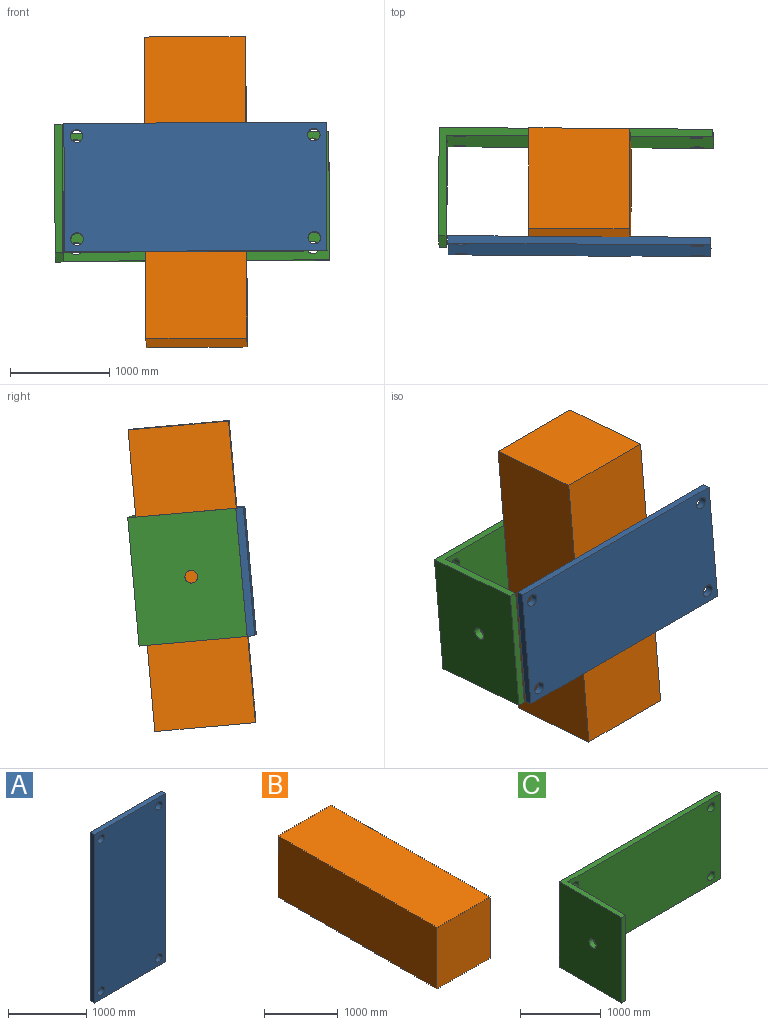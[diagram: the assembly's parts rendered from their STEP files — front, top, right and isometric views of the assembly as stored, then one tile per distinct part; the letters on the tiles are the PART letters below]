
ASSEMBLY  parts=3 mates=2
PART A: 10 faces, bbox 1295.4x76.2x2641.6 mm
  f0: plane 1295.4x76.2mm, normal (0,0,1), area 98709.5mm2, adj f1,f3,f4,f5
  f1: plane 2641.6x76.2mm, normal (-1,0,0), area 201289.9mm2, adj f0,f2,f4,f5
  f2: plane 1295.4x76.2mm, normal (0,0,-1), area 98709.5mm2, adj f1,f3,f4,f5
  f3: plane 2641.6x76.2mm, normal (1,0,0), area 201289.9mm2, adj f0,f2,f4,f5
  f4: plane 2641.6x1295.4mm, normal (0,-1,0), area 3371257.9mm2, adj f0,f1,f2,f3,f6,f7,f8,f9
  f5: plane 2641.6x1295.4mm, normal (0,1,0), area 3371257.9mm2, adj f0,f1,f2,f3,f6,f7,f8,f9
  f6: cylinder r=63.5mm len=127mm, axis (0,1,0), area 30402.4mm2, adj f4,f5
  f7: cylinder r=63.5mm len=127mm, axis (0,1,0), area 30402.4mm2, adj f4,f5
  f8: cylinder r=63.5mm len=127mm, axis (0,1,0), area 30402.4mm2, adj f4,f5
  f9: cylinder r=63.5mm len=127mm, axis (0,1,0), area 30402.4mm2, adj f4,f5
PART B: 6 faces, bbox 1016x3048x1016 mm
  f0: plane 3048x1016mm, normal (0,0,1), area 3096768mm2, adj f1,f3,f4,f5
  f1: plane 3048x1016mm, normal (-1,0,0), area 3096768mm2, adj f0,f2,f4,f5
  f2: plane 3048x1016mm, normal (0,0,-1), area 3096768mm2, adj f1,f3,f4,f5
  f3: plane 3048x1016mm, normal (1,0,0), area 3096768mm2, adj f0,f2,f4,f5
  f4: plane 1016x1016mm, normal (0,-1,0), area 1032256mm2, adj f0,f1,f2,f3
  f5: plane 1016x1016mm, normal (0,1,0), area 1032256mm2, adj f0,f1,f2,f3
PART C: 13 faces, bbox 2754.9x1092.2x1295.4 mm
  f0: plane 2678.71x1295.4mm, normal (0,-1,0), area 3419330.9mm2, adj f1,f3,f4,f6,f7,f8,f9,f10
  f1: plane 2754.91x1092.2mm, normal (0,0,1), area 287343.4mm2, adj f0,f2,f4,f5,f10,f11
  f2: plane 1295.4x1092.2mm, normal (-1,0,0), area 1402168.2mm2, adj f1,f3,f5,f11,f12
  f3: plane 2754.91x1092.2mm, normal (0,0,-1), area 287343.4mm2, adj f0,f2,f4,f5,f10,f11
  f4: plane 1295.4x76.2mm, normal (1,0,0), area 98709.5mm2, adj f0,f1,f3,f5
  f5: plane 2754.91x1295.4mm, normal (0,1,0), area 3518040.4mm2, adj f1,f2,f3,f4,f6,f7,f8,f9
  f6: cylinder r=63.5mm len=127mm, axis (0,1,0), area 30402.4mm2, adj f0,f5
  f7: cylinder r=63.5mm len=127mm, axis (0,1,0), area 30402.4mm2, adj f0,f5
  f8: cylinder r=63.5mm len=127mm, axis (0,1,0), area 30402.4mm2, adj f0,f5
  f9: cylinder r=63.5mm len=127mm, axis (0,1,0), area 30402.4mm2, adj f0,f5
  f10: plane 1295.4x1016mm, normal (1,0,0), area 1303458.7mm2, adj f0,f1,f3,f11,f12
  f11: plane 1295.4x76.2mm, normal (0,-1,0), area 98709.5mm2, adj f1,f2,f3,f10
  f12: cylinder r=63.5mm len=127mm, axis (1,0,0), area 30402.4mm2, adj f2,f10
PLACE A rot(axis=(0.71,-0.03,-0.7),176.7deg) t=(-930.55,-1008.45,95.15)mm
PLACE B rot(axis=(-0.6,-0.54,0.59),123deg) t=(-112.74,-1014.93,-779.78)mm fixed
PLACE C rot(axis=(-1,-0.06,-0.07),5.1deg) t=(88.06,220.97,803.29)mm
MATE fastened C.f0 <-> B.f3  axis (-0.01,-1,0.09) through (393.81,129,651.2)mm
MATE fastened A.f4 <-> B.f1  axis (0.01,1,-0.09) through (387.34,-882.99,741.12)mm
